# Revit family: Basic_Valves-Full_Port-WATTS-LFM1115_2in_Angle_150
name_source: partatom
category: Pipe Accessories
revit_build: Autodesk Revit 2016 (Build: 20150714_1515(x64)
units: mm (PartAtom-declared; Revit-internal decimal feet)

## family parameters
Always vertical = Yes
Cut with Voids When Loaded = No
OmniClass Number = 23.65.55.14
OmniClass Title = Valves for Liquid Services
Part Type = Valve - Breaks Into
Round Connector Dimension = Use Radius
Shared = Yes
Work Plane-Based = No

## types (1)
- LFM1115 - 2" (Angle 150#)
    Assembly Code = D2090600
    Body Radius = 1 1/2"
    Center to Top = 6 1/2"
    Connection Radius = 1"
    Connection Size = 2"
    Connection Type = 150#
    Country = United States
    Description = The Watts ACV Models M100 and M1100 are full port, single chamber basic valves that incorporate a one-piece disc and diaphragm assembly. This assembly is the only moving part within the valve allowing it to open, close, or modulate as commanded by the pilot control system.
    Flange Geometry = Yes
    Flange Radius = 2 1/2"
    Flange Thickness = 1/8"
    Horizontal Length(H,I,G) = 3 1/4"
    Inlet Connection Description = 2" Inlet Connection
    Inlet Dist. from Body = 1"
    K NPT Port Size = 3/8"
    K Port Location = 3/8"
    Manufacturer = WATTS
    Manufacturer Product Line = Automatic Control Valves
    Material = Metal-WATTS-Ductile Iron
    Model = M1100
    NPT Port Size K = 1/4"
    NPT Port Size K radius = 1/8"
    Nominal Dist. = 17/32"
    Nominal Height = 2 3/8"
    Nominal Radius 1 = 3/8"
    Nominal Radius 2 ( L ) = 1/2"
    Nominal Thickness = 5/8"
    Nominal Width = 3 1/4"
    Outlet Connection Description = 2" Outlet Connection
    Pressure Rating = 250.00 psi
    Price = Prices may vary. Please consult Manufacturer Representative for most up-to-date price list.
    Product Documentation Link = http://media.wattswater.com
    Product Page URL = https://www.watts.com
    Region = North America
    Top Port K Location = 1 3/32"
    URL = http://www.watts.com
    Vertical Length (E,F,G) = 4 3/4"
    Warranty Information = 1 Year (Limited)
    Weight = 40lbs./ 18kgs.

## geometry (parser evidence)
native form markers: Sweep x7
no freeform markers — native parametric forms only
